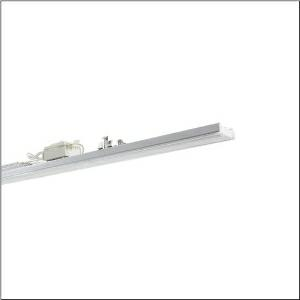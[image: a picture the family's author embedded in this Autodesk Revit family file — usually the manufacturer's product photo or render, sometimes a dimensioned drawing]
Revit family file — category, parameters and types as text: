
# Revit family: licross_r__21_recessed_mo_52tl11mn4a5g_bccd
name_source: partatom
category: Lighting Fixtures
units: mm (PartAtom-declared; Revit-internal decimal feet)

## family parameters
Cut with Voids When Loaded = No
Host = Face
Light Source = No
Part Type = Normal
Room Calculation Point = No
Round Connector Dimension = Use Diameter
Shared = No

## types (1)
- --- (1 x LED, 10830 lm, 60.5 W, 4000K)
    Apparent Load = 61 VA
    CIE Flux Codes = 89 96 99 100 100
    Color Rendering = 80
    Color Temperature = 4000K
    Default Elevation = 1800 mm
    Description = Licross® 21 Recessed MO, luminaire insert, of sheet steel, galvanised, coil coated, white, length: 1.500mm, width: 66mm, height: 67mm, LED rated luminous flux: 10.820lm, light colour: 840, control gear: ON/OFF Multilumen, with plug, 3-pole, with phase selection, mains connection: 220..240V, AC, 50/60Hz, rated input power: 61W, internal wiring halogen-free, primary light control with lens, of plastic, primary optical cover: cover, of PMMA, light emission: direct distribution, primary light characteristic: symmetric, protection rating (complete): IP40, insulation class (complete): insulation class I (protective earthing), certification: CE, ENEC, VDE, UKCA, protection symbol: D if used in an environment without relevant dust loads with corresponding accessories, impact resistance: IK06, permissible ambient temperature for indoor applications: -35..+40°C, corresponds to IFS (International Featured Standards) requirements for safety and quality in the food industry, reducing of maximum allowable ambient temperature of 5°C with ceiling mounting, LABS conformity tested according to VDMA 24364:2018-05, packaging unit: 1 piece
    Height = 58 mm
    Lamp = 1 x LED
    Lamp Light Flux = 10830 lm
    Lamp Power = 60.5 W
    Lamp count = 1
    Length = 1500 mm
    Luminous efficacy = 179 lm/W
    Manufacturer = Siteco
    ModVariant = No
    Model = 52TL11MN4A5G
    Mounting Place = Ceiling
    Mounting Type = Pendant
    Number of Poles = 1
    OnlyDefault = Yes
    Power Factor = 1
    Product Name = Licross® 21 Recessed MO
    Product group = luminaire insert | ceiling pendant
    ProductGroupID = 902
    Protection Class = Protection class I
    Protection Degree = IP 40
    RLX_Detail_Level = 1
    RLX_Emergency_Light_Flux = 0 lm
    RLX_Emergency_Type = 0
    RLX_Emergency_Type_DB = No
    RlxData = <blob elided: 22249 chars, md5=a44d0cf3>
    Socket = socket
    Standby Power = 0 W
    System Light Flux = 10830 lm
    System Power = 61 W
    Type Comments = factory setting: luminous flux: 100 % | (A | C | E) | 140 mA
    Type Image = l_1296930.jpg
    URL = http://relux.com
    VarID = @adj_129467
    Voltage = 0 V
    Weight = 0.00 kg
    Width = 66 mm

## geometry (parser evidence)
native form markers: Blend x4, Sweep x11
no freeform markers — native parametric forms only
